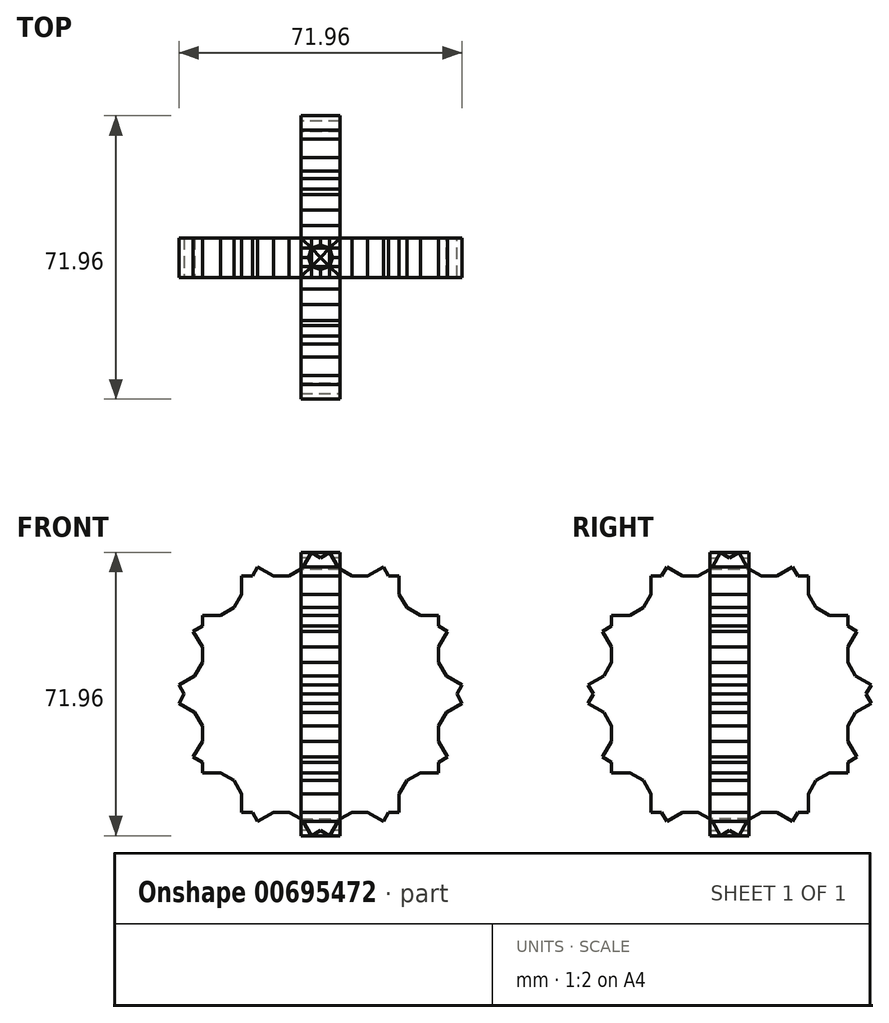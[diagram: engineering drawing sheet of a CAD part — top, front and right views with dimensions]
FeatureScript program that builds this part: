
annotation { "Feature Type Name" : "Feature", "Feature Type Description" : "" }
export const myFeature = defineFeature(function(context is Context, id is Id, definition is map)
    precondition{}
    {
        {
            var Q0;
            Q0=qCreatedBy(makeId("Front.planeOp"),FACE);
            var sketch = newSketch(context, id + "F0", { "sketchPlane" : qUnion([Q0])});
            skLineSegment(sketch, "E0.bottom", {"start": v(0, 0) * mm, "end": v(-30, 0) * mm});
            skLineSegment(sketch, "E0.top", {"start": v(-15, 40) * mm, "end": v(-30, 40) * mm});
            skLineSegment(sketch, "E0.left", {"start": v(0, 0) * mm, "end": v(0, 20) * mm});
            skLineSegment(sketch, "E0.right", {"start": v(-30, 0) * mm, "end": v(-30, 40) * mm});
            skArc(sketch, "E1", {"start": v(-15, 40) * mm, "mid": v(-17.5, 22.5) * mm, "end": v(0, 20) * mm});
            skPoint(sketch, "E1.midSnap0", {"position": v(0, 20) * mm});
            skPoint(sketch, "E1.midSnap1", {"position": v(-15, 40) * mm});
            skSolve(sketch);
        }
        {
            var Q0;
            Q0=makeQuery(id+"F0.imprint","IMPRINT",FACE,{"disambiguationData":[TD([[makeQuery(id+"F0.imprint","IMPRINT",EDGE,{"derivedFrom":sQuery(id+"F0.wireOp",EDGE,"E0.bottom")}),-1.0]])]});
            extrude(context, id + "F1", {"entities" : qUnion([Q0]), "depth" : 10 * mm, "offsetDistance" : 25 * mm, "symmetric" : true});
        }
        {
            var Q0;
            Q0=makeQuery(id+"F1.opExtrude","SWEPT_BODY",BODY,{"disambiguationData":[OSD([sQuery(id+"F0.wireOp",EDGE,"E0.bottom"),sQuery(id+"F0.wireOp",EDGE,"E0.top"),sQuery(id+"F0.wireOp",EDGE,"E0.left"),sQuery(id+"F0.wireOp",EDGE,"E0.right"),sQuery(id+"F0.wireOp",EDGE,"E1")])]});
            var Q1;
            Q1=makeQuery(id+"F1.opExtrude","SWEPT_EDGE",EDGE,{"disambiguationData":[OSD([sQuery(id+"F0.wireOp",EDGE,"E0.left"),sQuery(id+"F0.wireOp",EDGE,"E1")])]});
            circularPattern(context, id + "F2", {"operationType" : NewBodyOperationType.ADD, "entities" : qUnion([Q0]), "axis" : qUnion([Q1]), "angle" : 360 * degree, "instanceCount" : 12, "equalSpace" : true});
        }
        {
            var Q0;
            Q0=qCreatedBy(makeId("Right.planeOp"),FACE);
            var sketch = newSketch(context, id + "F3", { "sketchPlane" : qUnion([Q0])});
            skLineSegment(sketch, "E2.bottom", {"start": v(0.06, 0) * mm, "end": v(-29.94, 0) * mm});
            skLineSegment(sketch, "E2.top", {"start": v(-14.94, 40) * mm, "end": v(-29.94, 40) * mm});
            skLineSegment(sketch, "E2.left", {"start": v(0.06, 0) * mm, "end": v(0.06, 20) * mm});
            skLineSegment(sketch, "E2.right", {"start": v(-29.94, 0) * mm, "end": v(-29.94, 40) * mm});
            skArc(sketch, "E3", {"start": v(-14.94, 40) * mm, "mid": v(-17.44, 22.5) * mm, "end": v(0.06, 20) * mm});
            skPoint(sketch, "E3.midSnap0", {"position": v(0.06, 20) * mm});
            skPoint(sketch, "E3.midSnap1", {"position": v(-14.94, 40) * mm});
            skSolve(sketch);
        }
        {
            var Q0;
            Q0=makeQuery(id+"F3.imprint","IMPRINT",FACE,{"disambiguationData":[TD([[makeQuery(id+"F3.imprint","IMPRINT",EDGE,{"derivedFrom":sQuery(id+"F3.wireOp",EDGE,"E2.bottom")}),-1.0]])]});
            extrude(context, id + "F4", {"entities" : qUnion([Q0]), "depth" : 10 * mm, "offsetDistance" : 25 * mm, "symmetric" : true});
        }
        {
            var Q0;
            Q0=makeQuery(id+"F4.opExtrude","SWEPT_BODY",BODY,{"disambiguationData":[OSD([sQuery(id+"F3.wireOp",EDGE,"E2.bottom"),sQuery(id+"F3.wireOp",EDGE,"E2.top"),sQuery(id+"F3.wireOp",EDGE,"E2.left"),sQuery(id+"F3.wireOp",EDGE,"E2.right"),sQuery(id+"F3.wireOp",EDGE,"E3")])]});
            var Q1;
            Q1=makeQuery(id+"F4.opExtrude","SWEPT_EDGE",EDGE,{"disambiguationData":[OSD([sQuery(id+"F3.wireOp",EDGE,"E2.left"),sQuery(id+"F3.wireOp",EDGE,"E3")])]});
            circularPattern(context, id + "F5", {"operationType" : NewBodyOperationType.ADD, "entities" : qUnion([Q0]), "axis" : qUnion([Q1]), "angle" : 360 * degree, "instanceCount" : 12, "equalSpace" : true});
        }
    });
